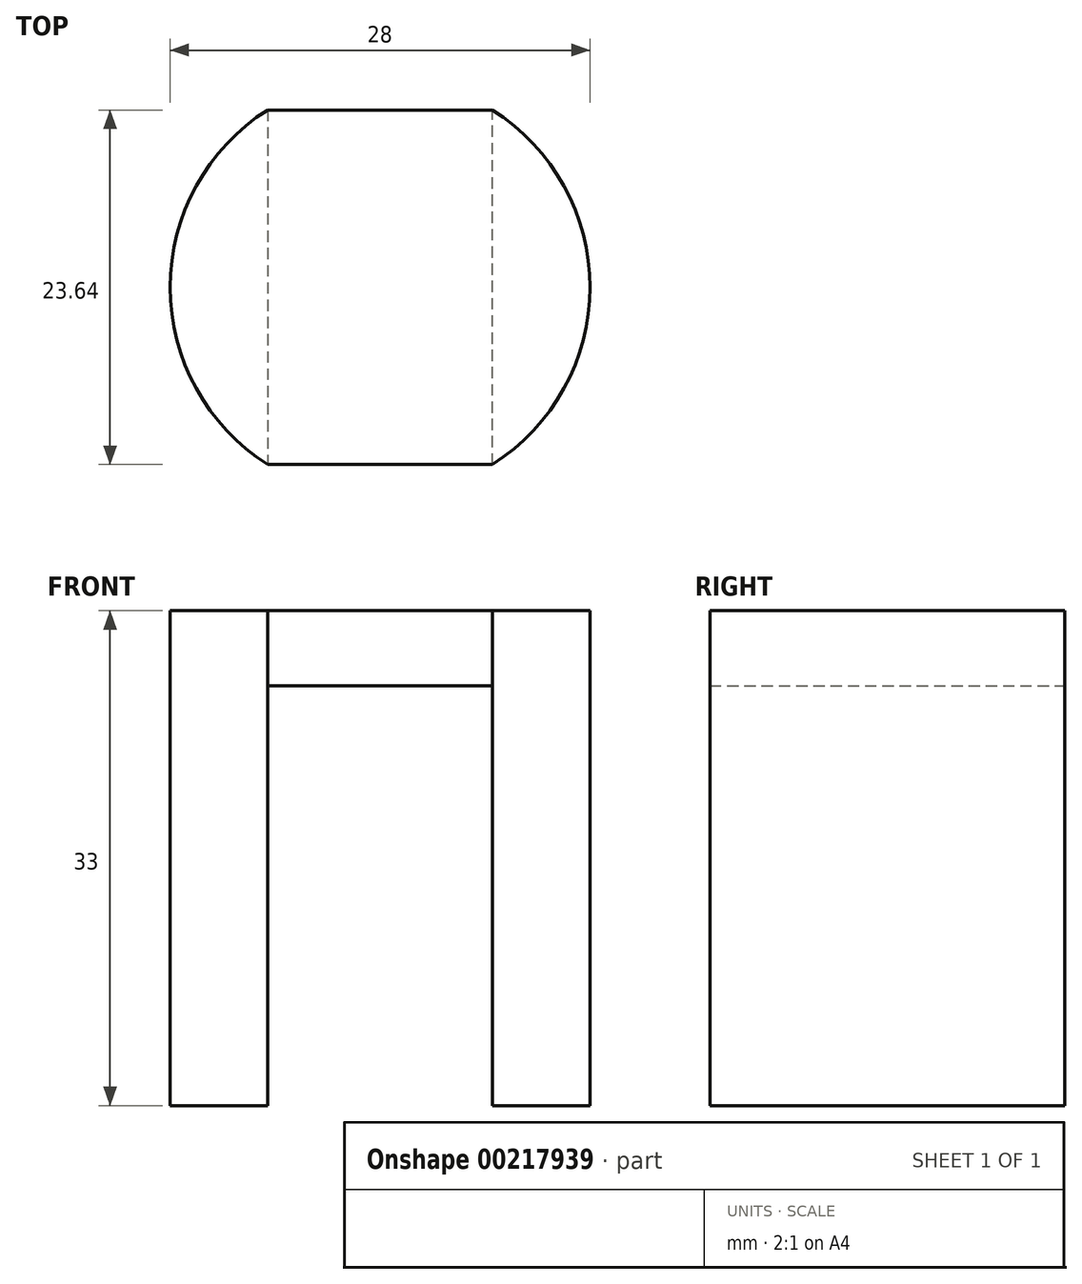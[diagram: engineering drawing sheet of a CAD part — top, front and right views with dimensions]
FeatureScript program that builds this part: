
annotation { "Feature Type Name" : "Feature", "Feature Type Description" : "" }
export const myFeature = defineFeature(function(context is Context, id is Id, definition is map)
    precondition{}
    {
        {
            var Q0;
            Q0=qCreatedBy(makeId("Top.planeOp"),FACE);
            var sketch = newSketch(context, id + "F0", { "sketchPlane" : qUnion([Q0])});
            skCircle(sketch, "E0", {"center": v(0, 0) * mm, "radius": 14 * mm});
            skCircle(sketch, "E1", {"center": v(0, 0) * mm, "radius": 5 * mm});
            skLineSegment(sketch, "E2", {"start": v(0, 0) * mm, "end": v(-7.5, 0) * mm});
            skLineSegment(sketch, "E3", {"start": v(0, 0) * mm, "end": v(7.5, 0) * mm});
            skLineSegment(sketch, "E4", {"start": v(7.5, 0) * mm, "end": v(7.5, 11.82) * mm});
            skLineSegment(sketch, "E5", {"start": v(7.5, 0) * mm, "end": v(7.5, -11.82) * mm});
            skLineSegment(sketch, "E6", {"start": v(-7.5, 0) * mm, "end": v(-7.5, 11.82) * mm});
            skLineSegment(sketch, "E7", {"start": v(-7.5, 0) * mm, "end": v(-7.5, -11.82) * mm});
            skLineSegment(sketch, "E8", {"start": v(-7.5, -11.82) * mm, "end": v(7.5, -11.82) * mm});
            skLineSegment(sketch, "E9", {"start": v(7.5, 11.82) * mm, "end": v(-7.5, 11.82) * mm});
            skSolve(sketch);
        }
        {
            var Q0;
            {var subQ0=sQuery(id+"F0.wireOp",EDGE,"E6");Q0=makeQuery(id+"F0.imprint","IMPRINT",FACE,{"disambiguationData":[TD([[makeQuery(id+"F0.imprint","IMPRINT",EDGE,{"derivedFrom":subQ0}),1.0]])]});}
            var Q1;
            {var subQ0=sQuery(id+"F0.wireOp",EDGE,"E5");Q1=makeQuery(id+"F0.imprint","IMPRINT",FACE,{"disambiguationData":[TD([[makeQuery(id+"F0.imprint","IMPRINT",EDGE,{"derivedFrom":subQ0}),-1.0]])]});}
            var Q2;
            {var subQ0=sQuery(id+"F0.wireOp",EDGE,"E4");Q2=makeQuery(id+"F0.imprint","IMPRINT",FACE,{"disambiguationData":[TD([[makeQuery(id+"F0.imprint","IMPRINT",EDGE,{"derivedFrom":subQ0}),1.0]])]});}
            var Q3;
            {var subQ0=sQuery(id+"F0.wireOp",EDGE,"E4");Q3=makeQuery(id+"F0.imprint","IMPRINT",FACE,{"disambiguationData":[TD([[makeQuery(id+"F0.imprint","IMPRINT",EDGE,{"derivedFrom":subQ0}),-1.0]])]});}
            var Q4;
            {var subQ0=sQuery(id+"F0.wireOp",EDGE,"E2");var subQ1=sQuery(id+"F0.wireOp",EDGE,"E1");var subQ2=makeQuery(id+"F0.imprint","INTERSECT",VERTEX,{"derivedFrom":[subQ1,subQ0]});Q4=makeQuery(id+"F0.imprint","IMPRINT",FACE,{"disambiguationData":[TD([[makeQuery(id+"F0.imprint","IMPRINT",EDGE,{"disambiguationData":[TD([[subQ2,-1.0]])],"derivedFrom":subQ1}),1.0]])]});}
            var Q5;
            {var subQ0=sQuery(id+"F0.wireOp",EDGE,"E2");var subQ1=sQuery(id+"F0.wireOp",EDGE,"E1");var subQ2=makeQuery(id+"F0.imprint","INTERSECT",VERTEX,{"derivedFrom":[subQ1,subQ0]});Q5=makeQuery(id+"F0.imprint","IMPRINT",FACE,{"disambiguationData":[TD([[makeQuery(id+"F0.imprint","IMPRINT",EDGE,{"disambiguationData":[TD([[subQ2,1.0]])],"derivedFrom":subQ1}),1.0]])]});}
            extrude(context, id + "F1", {"entities" : qUnion([Q0, Q1, Q2, Q3, Q4, Q5]), "depth" : 5 * mm});
        }
        {
            var Q0;
            {var subQ0=sQuery(id+"F0.wireOp",EDGE,"E6");Q0=makeQuery(id+"F0.imprint","IMPRINT",FACE,{"disambiguationData":[TD([[makeQuery(id+"F0.imprint","IMPRINT",EDGE,{"derivedFrom":subQ0}),1.0]])]});}
            var Q1;
            {var subQ0=sQuery(id+"F0.wireOp",EDGE,"E4");Q1=makeQuery(id+"F0.imprint","IMPRINT",FACE,{"disambiguationData":[TD([[makeQuery(id+"F0.imprint","IMPRINT",EDGE,{"derivedFrom":subQ0}),-1.0]])]});}
            extrude(context, id + "F2", {"entities" : qUnion([Q0, Q1]), "operationType" : NewBodyOperationType.ADD, "oppositeDirection" : true, "depth" : 28 * mm});
        }
    });
